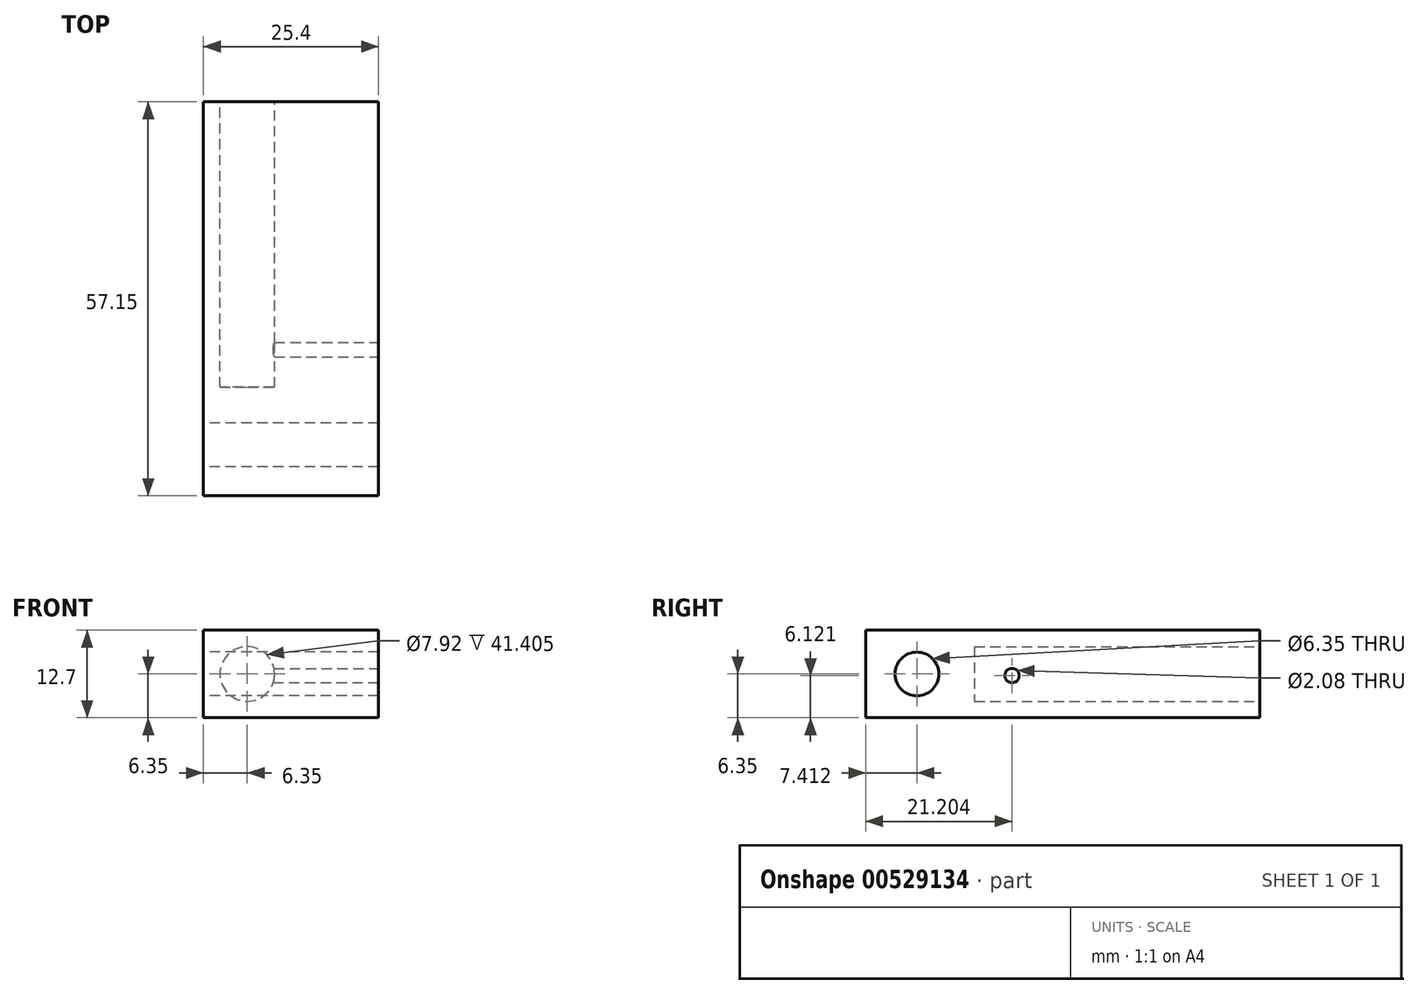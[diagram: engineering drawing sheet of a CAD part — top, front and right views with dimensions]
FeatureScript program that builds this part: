
annotation { "Feature Type Name" : "Feature", "Feature Type Description" : "" }
export const myFeature = defineFeature(function(context is Context, id is Id, definition is map)
    precondition{}
    {
        {
            var Q0;
            Q0=qCreatedBy(makeId("Top.planeOp"),FACE);
            var sketch = newSketch(context, id + "F0", { "sketchPlane" : qUnion([Q0])});
            skLineSegment(sketch, "E0.bottom", {"start": v(-12.7, 28.58) * mm, "end": v(12.7, 28.58) * mm});
            skLineSegment(sketch, "E0.top", {"start": v(-12.7, -28.57) * mm, "end": v(12.7, -28.57) * mm});
            skLineSegment(sketch, "E0.left", {"start": v(-12.7, 28.58) * mm, "end": v(-12.7, -28.57) * mm});
            skLineSegment(sketch, "E0.right", {"start": v(12.7, 28.58) * mm, "end": v(12.7, -28.57) * mm});
            skPoint(sketch, "E0.middle", {"position": v(0, 0) * mm});
            skSolve(sketch);
        }
        {
            var Q0;
            Q0 = qSketchRegion(id + "F0", true);
            extrude(context, id + "F1", {"entities" : qUnion([Q0]), "depth" : 12.7 * mm, "offsetDistance" : 25.4 * mm});
        }
        {
            var Q0;
            Q0=makeQuery(id+"F1.opExtrude","SWEPT_FACE",FACE,{"disambiguationData":[OSD([sQuery(id+"F0.wireOp",EDGE,"E0.left")])]});
            var sketch = newSketch(context, id + "F2", { "sketchPlane" : qUnion([Q0])});
            skLineSegment(sketch, "E1", {"start": v(-28.58, 6.35) * mm, "end": v(28.57, 6.35) * mm, "construction": true});
            skCircle(sketch, "E2", {"center": v(21.16, 6.35) * mm, "radius": 3.18 * mm});
            skSolve(sketch);
        }
        {
            var Q0;
            Q0 = qSketchRegion(id + "F2", true);
            extrude(context, id + "F3", {"entities" : qUnion([Q0]), "operationType" : NewBodyOperationType.REMOVE, "oppositeDirection" : true, "depth" : 30.8 * mm, "offsetDistance" : 25.4 * mm});
        }
        {
            var Q0;
            Q0=makeQuery(id+"F1.opExtrude","SWEPT_FACE",FACE,{"disambiguationData":[OSD([sQuery(id+"F0.wireOp",EDGE,"E0.bottom")])]});
            var sketch = newSketch(context, id + "F4", { "sketchPlane" : qUnion([Q0])});
            skCircle(sketch, "E3", {"center": v(6.35, 6.35) * mm, "radius": 3.96 * mm});
            skSolve(sketch);
        }
        {
            var Q0;
            Q0 = qSketchRegion(id + "F4", true);
            extrude(context, id + "F5", {"entities" : qUnion([Q0]), "operationType" : NewBodyOperationType.REMOVE, "oppositeDirection" : true, "depth" : 41.4 * mm, "offsetDistance" : 25.4 * mm});
        }
        {
            var Q0;
            Q0=makeQuery(id+"F1.opExtrude","SWEPT_FACE",FACE,{"disambiguationData":[OSD([sQuery(id+"F0.wireOp",EDGE,"E0.right")])]});
            var sketch = newSketch(context, id + "F6", { "sketchPlane" : qUnion([Q0])});
            skCircle(sketch, "E4", {"center": v(-7.37, 6.12) * mm, "radius": 1.04 * mm});
            skSolve(sketch);
        }
        {
            var Q0;
            Q0 = qSketchRegion(id + "F6", true);
            extrude(context, id + "F7", {"entities" : qUnion([Q0]), "operationType" : NewBodyOperationType.REMOVE, "oppositeDirection" : true, "depth" : 16.94 * mm, "offsetDistance" : 25.4 * mm});
        }
    });
